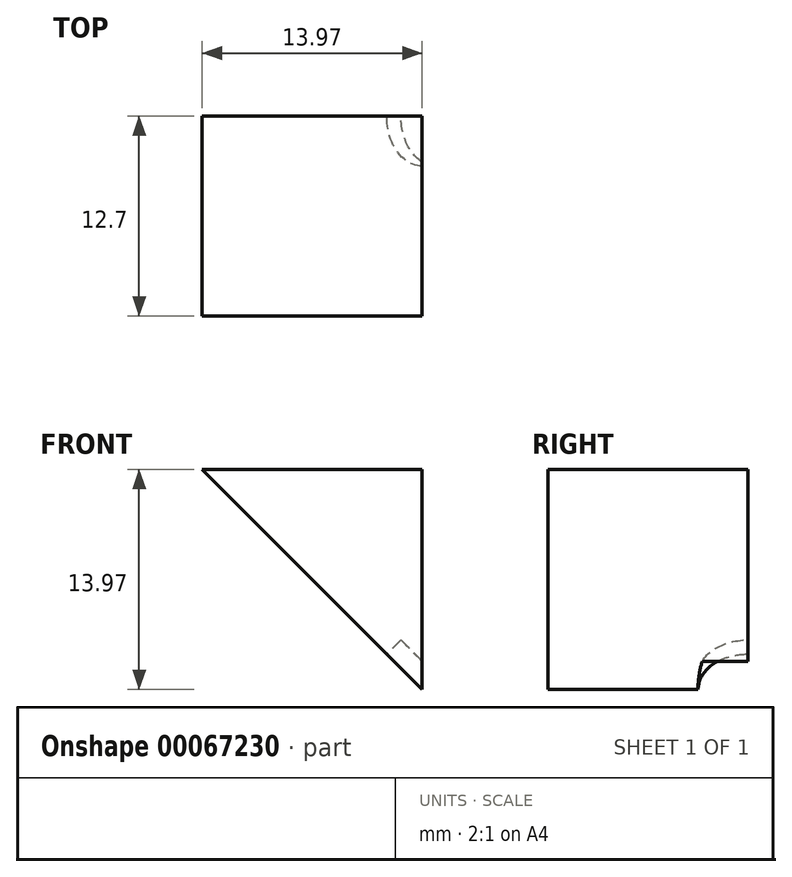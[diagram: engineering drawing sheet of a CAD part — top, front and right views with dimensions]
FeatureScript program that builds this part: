
annotation { "Feature Type Name" : "Feature", "Feature Type Description" : "" }
export const myFeature = defineFeature(function(context is Context, id is Id, definition is map)
    precondition{}
    {
        {
            var Q0;
            Q0=qCreatedBy(makeId("Front.planeOp"),FACE);
            var sketch = newSketch(context, id + "F0", { "sketchPlane" : qUnion([Q0])});
            skLineSegment(sketch, "E0", {"start": v(0, 0) * mm, "end": v(-25.4, 25.4) * mm});
            skLineSegment(sketch, "E1", {"start": v(-25.4, 25.4) * mm, "end": v(0, 25.4) * mm});
            skLineSegment(sketch, "E2", {"start": v(0, 25.4) * mm, "end": v(0, 0) * mm});
            skSolve(sketch);
        }
        {
            var Q0;
            Q0=makeQuery(id+"F0.imprint","IMPRINT",FACE,{"disambiguationData":[TD([[makeQuery(id+"F0.imprint","IMPRINT",EDGE,{"derivedFrom":sQuery(id+"F0.wireOp",EDGE,"E0")}),-1.0]])]});
            extrude(context, id + "F1", {"entities" : qUnion([Q0]), "depth" : 12.7 * mm, "symmetric" : true});
        }
        {
            var Q0;
            Q0=makeQuery(id+"F1.opExtrude","SWEPT_FACE",FACE,{"disambiguationData":[OSD([sQuery(id+"F0.wireOp",EDGE,"E0")])]});
            var sketch = newSketch(context, id + "F2", { "sketchPlane" : qUnion([Q0])});
            skCircle(sketch, "E3", {"center": v(-6.35, 0) * mm, "radius": 3.18 * mm});
            skCircle(sketch, "E4", {"center": v(-13.97, 0) * mm, "radius": 3.18 * mm});
            skSolve(sketch);
        }
        {
            var Q0;
            Q0=makeQuery(id+"F2.imprint","IMPRINT",FACE,{"disambiguationData":[TD([[makeQuery(id+"F2.imprint","IMPRINT",EDGE,{"derivedFrom":sQuery(id+"F2.wireOp",EDGE,"E4")}),1.0]])]});
            var Q1;
            Q1=makeQuery(id+"F2.imprint","IMPRINT",FACE,{"disambiguationData":[TD([[makeQuery(id+"F2.imprint","IMPRINT",EDGE,{"derivedFrom":sQuery(id+"F2.wireOp",EDGE,"E3")}),1.0]])]});
            extrude(context, id + "F3", {"entities" : qUnion([Q0, Q1]), "operationType" : NewBodyOperationType.REMOVE, "oppositeDirection" : true, "depth" : 1.27 * mm});
        }
        {
            var Q0;
            Q0=makeQuery(id+"F1.opExtrude","CAP_FACE",FACE,{"disambiguationData":[OSD([sQuery(id+"F0.wireOp",EDGE,"E0"),sQuery(id+"F0.wireOp",EDGE,"E1"),sQuery(id+"F0.wireOp",EDGE,"E2")])],"isStart":false});
            var sketch = newSketch(context, id + "F4", { "sketchPlane" : qUnion([Q0])});
            skLineSegment(sketch, "E5", {"start": v(-13.97, 13.97) * mm, "end": v(0, 13.97) * mm});
            skLineSegment(sketch, "E6", {"start": v(0, 13.97) * mm, "end": v(0, 25.4) * mm});
            skLineSegment(sketch, "E7", {"start": v(0, 25.4) * mm, "end": v(-25.4, 25.4) * mm});
            skLineSegment(sketch, "E8", {"start": v(-25.4, 25.4) * mm, "end": v(-13.97, 13.97) * mm});
            skSolve(sketch);
        }
        {
            var Q0;
            Q0=makeQuery(id+"F4.imprint","IMPRINT",FACE,{"disambiguationData":[TD([[makeQuery(id+"F4.imprint","IMPRINT",EDGE,{"derivedFrom":sQuery(id+"F4.wireOp",EDGE,"E5")}),1.0]])]});
            extrude(context, id + "F5", {"entities" : qUnion([Q0]), "operationType" : NewBodyOperationType.REMOVE, "oppositeDirection" : true, "depth" : 12.7 * mm});
        }
    });
